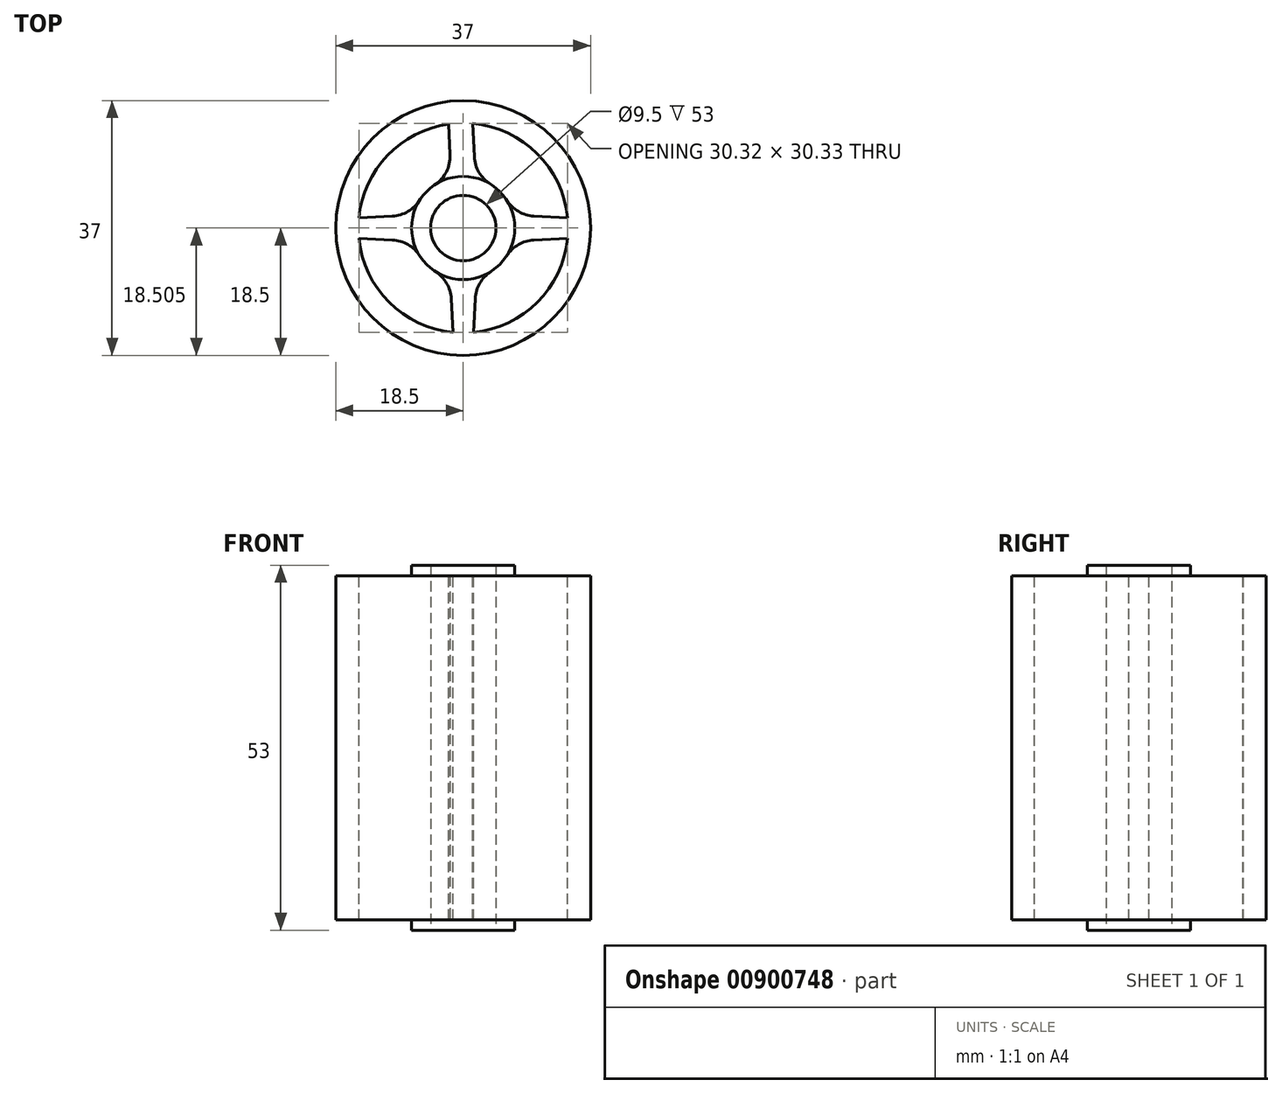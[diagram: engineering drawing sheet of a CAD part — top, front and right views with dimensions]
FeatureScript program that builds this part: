
annotation { "Feature Type Name" : "Feature", "Feature Type Description" : "" }
export const myFeature = defineFeature(function(context is Context, id is Id, definition is map)
    precondition{}
    {
        {
            var Q0;
            Q0=qCreatedBy(makeId("Top.planeOp"),FACE);
            var sketch = newSketch(context, id + "F0", { "sketchPlane" : qUnion([Q0])});
            skCircle(sketch, "E0", {"center": v(0, 0) * mm, "radius": 4.75 * mm});
            skCircle(sketch, "E1", {"center": v(0, 0) * mm, "radius": 7.5 * mm});
            skSolve(sketch);
        }
        {
            var Q0;
            Q0 = qSketchRegion(id + "F0", true);
            extrude(context, id + "F1", {"entities" : qUnion([Q0]), "endBound" : BoundingType.SYMMETRIC, "depth" : 53 * mm, "offsetDistance" : 25 * mm});
        }
        {
            var Q0;
            Q0=qCreatedBy(makeId("Top.planeOp"),FACE);
            var sketch = newSketch(context, id + "F2", { "sketchPlane" : qUnion([Q0])});
            skCircle(sketch, "E2", {"center": v(0, 0) * mm, "radius": 18.5 * mm});
            skCircle(sketch, "E3", {"center": v(0, 0) * mm, "radius": 5.83 * mm});
            skSolve(sketch);
        }
        {
            var Q0;
            Q0=makeQuery(id+"F2.imprint","IMPRINT",FACE,{"disambiguationData":[TD([[makeQuery(id+"F2.imprint","IMPRINT",EDGE,{"derivedFrom":sQuery(id+"F2.wireOp",EDGE,"E2")}),1.0]])]});
            extrude(context, id + "F3", {"entities" : qUnion([Q0]), "operationType" : NewBodyOperationType.ADD, "endBound" : BoundingType.SYMMETRIC, "depth" : 50 * mm, "offsetDistance" : 25 * mm});
        }
        {
            var Q0;
            Q0=makeQuery(id+"F3.opExtrude","CAP_FACE",FACE,{"disambiguationData":[OSD([sQuery(id+"F2.wireOp",EDGE,"E2"),sQuery(id+"F2.wireOp",EDGE,"E3")])],"isStart":false});
            var sketch = newSketch(context, id + "F4", { "sketchPlane" : qUnion([Q0])});
            skArc(sketch, "E4", {"start": v(-15.16, -1.48) * mm, "mid": v(-10.77, -10.77) * mm, "end": v(-1.48, -15.16) * mm});
            skLineSegment(sketch, "E5", {"start": v(0, 0) * mm, "end": v(0, 0.07) * mm});
            skLineSegment(sketch, "E6.left", {"start": v(-2.13, 15.08) * mm, "end": v(-1.75, 7.3) * mm});
            skLineSegment(sketch, "E6.right", {"start": v(1.37, 15.17) * mm, "end": v(1.75, 7.3) * mm});
            skPoint(sketch, "E6.middle", {"position": v(0, 7.62) * mm});
            skLineSegment(sketch, "E7.1.0", {"start": v(-15.16, 1.48) * mm, "end": v(-7.26, 1.88) * mm});
            skLineSegment(sketch, "E7.1.1", {"start": v(-15.16, -1.48) * mm, "end": v(-7.26, -1.88) * mm});
            skLineSegment(sketch, "E7.2.0", {"start": v(-1.48, -15.16) * mm, "end": v(-1.88, -7.26) * mm});
            skLineSegment(sketch, "E7.2.1", {"start": v(1.48, -15.16) * mm, "end": v(1.88, -7.26) * mm});
            skLineSegment(sketch, "E7.3.0", {"start": v(15.16, -1.48) * mm, "end": v(7.26, -1.88) * mm});
            skLineSegment(sketch, "E7.3.1", {"start": v(15.16, 1.48) * mm, "end": v(7.26, 1.88) * mm});
            skArc(sketch, "E8", {"start": v(-7.26, -1.88) * mm, "mid": v(-5.3, -5.3) * mm, "end": v(-1.88, -7.26) * mm});
            skPoint(sketch, "E9.orphan", {"position": v(-1.64, -2.17) * mm});
            skPoint(sketch, "E10.orphan", {"position": v(-2.17, -1.64) * mm});
            skPoint(sketch, "E11.orphan", {"position": v(2.17, -1.64) * mm});
            skPoint(sketch, "E12.trimOffspring.end.orphan", {"position": v(-1.37, 0.06) * mm});
            skPoint(sketch, "E6.top.end.orphan", {"position": v(2.13, 0.15) * mm});
            skArc(sketch, "E13.trimOffspring", {"start": v(1.88, -7.26) * mm, "mid": v(5.3, -5.3) * mm, "end": v(7.26, -1.88) * mm});
            skArc(sketch, "E14.trimOffspring", {"start": v(1.48, -15.16) * mm, "mid": v(10.77, -10.77) * mm, "end": v(15.16, -1.48) * mm});
            skPoint(sketch, "E15.trimOffspring.end.orphan", {"position": v(0, 15.23) * mm});
            skArc(sketch, "E16.trimOffspring", {"start": v(-2.13, 15.08) * mm, "mid": v(-11, 10.54) * mm, "end": v(-15.16, 1.48) * mm});
            skArc(sketch, "E17.trimOffspring", {"start": v(-1.75, 7.3) * mm, "mid": v(-5.26, 5.35) * mm, "end": v(-7.26, 1.88) * mm});
            skArc(sketch, "E18.trimOffspring", {"start": v(7.26, 1.88) * mm, "mid": v(5.25, 5.35) * mm, "end": v(1.75, 7.3) * mm});
            skArc(sketch, "E19.trimOffspring", {"start": v(15.16, 1.48) * mm, "mid": v(10.73, 10.8) * mm, "end": v(1.37, 15.17) * mm});
            skSolve(sketch);
        }
        {
            var Q0;
            Q0=makeQuery(id+"F4.imprint","IMPRINT",FACE,{"disambiguationData":[TD([[makeQuery(id+"F4.imprint","IMPRINT",EDGE,{"derivedFrom":sQuery(id+"F4.wireOp",EDGE,"E6.left")}),-1.0]])]});
            var Q1;
            Q1=makeQuery(id+"F4.imprint","IMPRINT",FACE,{"disambiguationData":[TD([[makeQuery(id+"F4.imprint","IMPRINT",EDGE,{"derivedFrom":sQuery(id+"F4.wireOp",EDGE,"E6.right")}),1.0]])]});
            var Q2;
            Q2=makeQuery(id+"F4.imprint","IMPRINT",FACE,{"disambiguationData":[TD([[makeQuery(id+"F4.imprint","IMPRINT",EDGE,{"derivedFrom":sQuery(id+"F4.wireOp",EDGE,"E7.2.1")}),-1.0]])]});
            var Q3;
            Q3=makeQuery(id+"F4.imprint","IMPRINT",FACE,{"disambiguationData":[TD([[makeQuery(id+"F4.imprint","IMPRINT",EDGE,{"derivedFrom":sQuery(id+"F4.wireOp",EDGE,"E4")}),1.0]])]});
            extrude(context, id + "F5", {"entities" : qUnion([Q0, Q1, Q2, Q3]), "operationType" : NewBodyOperationType.REMOVE, "endBound" : BoundingType.THROUGH_ALL, "oppositeDirection" : true, "depth" : 25 * mm, "offsetDistance" : 25 * mm});
        }
        {
            var Q0;
            Q0=makeQuery(id+"F5.boolean.opBoolean","COPY",EDGE,{"derivedFrom":makeQuery(id+"F5.opExtrude","SWEPT_EDGE",EDGE,{"disambiguationData":[OSD([sQuery(id+"F0.wireOp",EDGE,"E1"),sQuery(id+"F2.wireOp",EDGE,"E2"),sQuery(id+"F2.wireOp",EDGE,"E3"),sQuery(id+"F4.wireOp",EDGE,"E7.1.1"),sQuery(id+"F4.wireOp",EDGE,"E8")])]})});
            var Q1;
            Q1=makeQuery(id+"F5.boolean.opBoolean","COPY",EDGE,{"derivedFrom":makeQuery(id+"F5.opExtrude","SWEPT_EDGE",EDGE,{"disambiguationData":[OSD([sQuery(id+"F0.wireOp",EDGE,"E1"),sQuery(id+"F2.wireOp",EDGE,"E2"),sQuery(id+"F2.wireOp",EDGE,"E3"),sQuery(id+"F4.wireOp",EDGE,"E7.2.0"),sQuery(id+"F4.wireOp",EDGE,"E8")])]})});
            var Q2;
            Q2=makeQuery(id+"F5.boolean.opBoolean","COPY",EDGE,{"derivedFrom":makeQuery(id+"F5.opExtrude","SWEPT_EDGE",EDGE,{"disambiguationData":[OSD([sQuery(id+"F0.wireOp",EDGE,"E1"),sQuery(id+"F2.wireOp",EDGE,"E2"),sQuery(id+"F2.wireOp",EDGE,"E3"),sQuery(id+"F4.wireOp",EDGE,"E7.3.0"),sQuery(id+"F4.wireOp",EDGE,"E13.trimOffspring")])]})});
            var Q3;
            Q3=makeQuery(id+"F5.boolean.opBoolean","COPY",EDGE,{"derivedFrom":makeQuery(id+"F5.opExtrude","SWEPT_EDGE",EDGE,{"disambiguationData":[OSD([sQuery(id+"F0.wireOp",EDGE,"E1"),sQuery(id+"F2.wireOp",EDGE,"E2"),sQuery(id+"F2.wireOp",EDGE,"E3"),sQuery(id+"F4.wireOp",EDGE,"E7.3.1"),sQuery(id+"F4.wireOp",EDGE,"E18.trimOffspring")])]})});
            var Q4;
            Q4=makeQuery(id+"F5.boolean.opBoolean","COPY",EDGE,{"derivedFrom":makeQuery(id+"F5.opExtrude","SWEPT_EDGE",EDGE,{"disambiguationData":[OSD([sQuery(id+"F0.wireOp",EDGE,"E1"),sQuery(id+"F2.wireOp",EDGE,"E2"),sQuery(id+"F2.wireOp",EDGE,"E3"),sQuery(id+"F4.wireOp",EDGE,"E6.right"),sQuery(id+"F4.wireOp",EDGE,"E18.trimOffspring")])]})});
            var Q5;
            Q5=makeQuery(id+"F5.boolean.opBoolean","COPY",EDGE,{"derivedFrom":makeQuery(id+"F5.opExtrude","SWEPT_EDGE",EDGE,{"disambiguationData":[OSD([sQuery(id+"F0.wireOp",EDGE,"E1"),sQuery(id+"F2.wireOp",EDGE,"E2"),sQuery(id+"F2.wireOp",EDGE,"E3"),sQuery(id+"F4.wireOp",EDGE,"E7.2.1"),sQuery(id+"F4.wireOp",EDGE,"E13.trimOffspring")])]})});
            var Q6;
            Q6=makeQuery(id+"F5.boolean.opBoolean","COPY",EDGE,{"derivedFrom":makeQuery(id+"F5.opExtrude","SWEPT_EDGE",EDGE,{"disambiguationData":[OSD([sQuery(id+"F0.wireOp",EDGE,"E1"),sQuery(id+"F2.wireOp",EDGE,"E2"),sQuery(id+"F2.wireOp",EDGE,"E3"),sQuery(id+"F4.wireOp",EDGE,"E7.1.0"),sQuery(id+"F4.wireOp",EDGE,"E17.trimOffspring")])]})});
            var Q7;
            Q7=makeQuery(id+"F5.boolean.opBoolean","COPY",EDGE,{"derivedFrom":makeQuery(id+"F5.opExtrude","SWEPT_EDGE",EDGE,{"disambiguationData":[OSD([sQuery(id+"F0.wireOp",EDGE,"E1"),sQuery(id+"F2.wireOp",EDGE,"E2"),sQuery(id+"F2.wireOp",EDGE,"E3"),sQuery(id+"F4.wireOp",EDGE,"E6.left"),sQuery(id+"F4.wireOp",EDGE,"E17.trimOffspring")])]})});
            fillet(context, id + "F6", {"entities" : qUnion([Q0, Q1, Q2, Q3, Q4, Q5, Q6, Q7]), "radius" : 5 * mm, "tangentPropagation" : true, "allowEdgeOverflow" : false});
        }
    });
